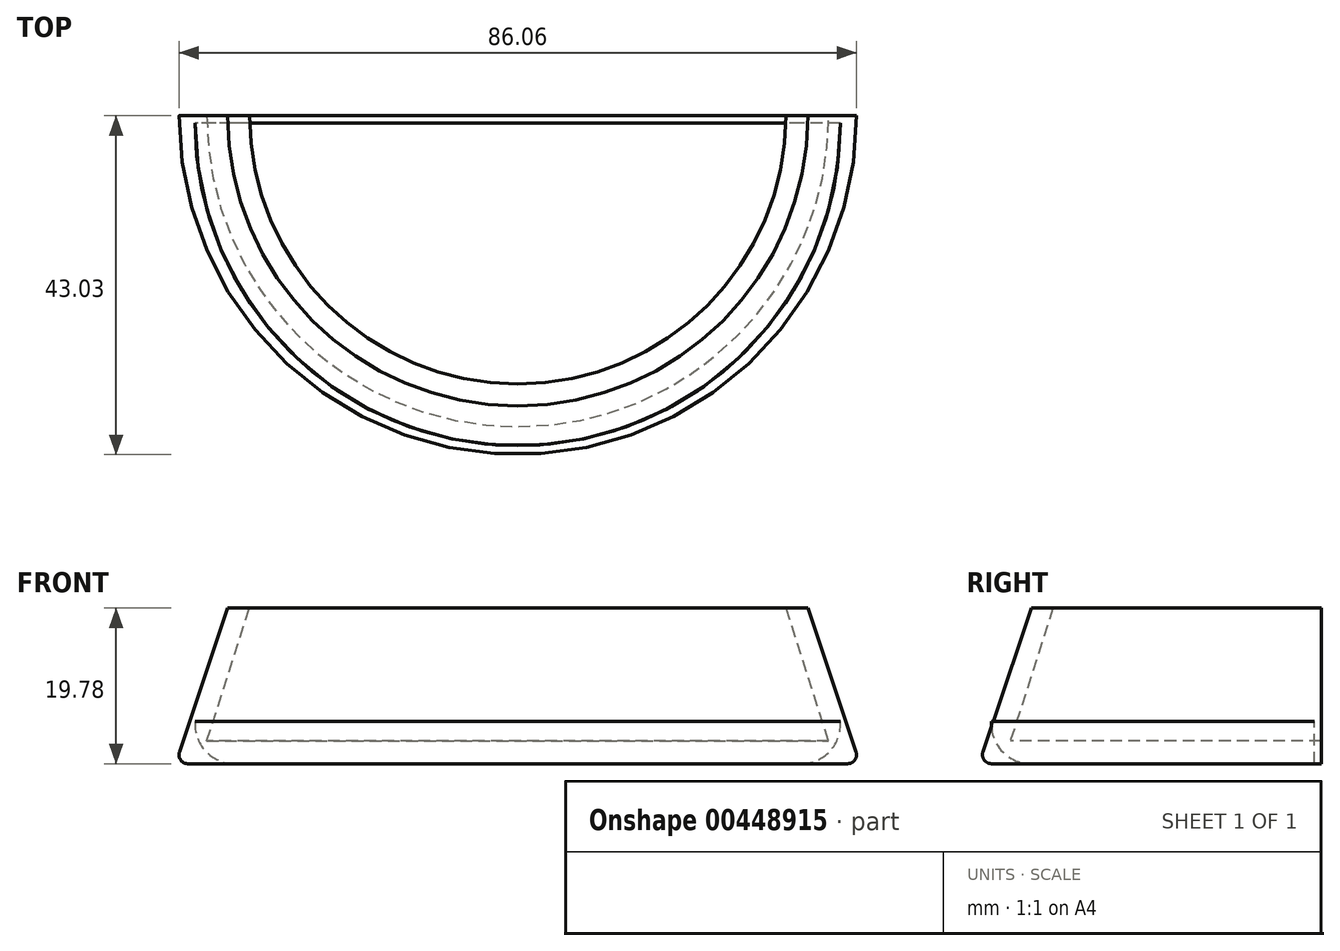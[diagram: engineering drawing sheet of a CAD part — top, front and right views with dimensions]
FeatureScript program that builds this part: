
annotation { "Feature Type Name" : "Feature", "Feature Type Description" : "" }
export const myFeature = defineFeature(function(context is Context, id is Id, definition is map)
    precondition{}
    {
        {
            var Q0;
            Q0=qCreatedBy(makeId("Front.planeOp"),FACE);
            cPlane(context, id + "F0", {"entities" : qUnion([Q0]), "cplaneType" : CPlaneType.OFFSET, "offset" : 0.9 * mm, "width" : 150 * mm, "height" : 150 * mm});
        }
        {
            var Q0;
            Q0=qCreatedBy(makeId("Front.planeOp"),FACE);
            var sketch = newSketch(context, id + "F1", { "sketchPlane" : qUnion([Q0])});
            skLineSegment(sketch, "E0", {"start": v(-43.47, 0) * mm, "end": v(0, 0) * mm});
            skLineSegment(sketch, "E1", {"start": v(0, 0) * mm, "end": v(0, 2.9) * mm});
            skLineSegment(sketch, "E2", {"start": v(0, 2.9) * mm, "end": v(-39.5, 2.9) * mm});
            skLineSegment(sketch, "E3", {"start": v(-39.5, 2.9) * mm, "end": v(-34.07, 19.78) * mm});
            skLineSegment(sketch, "E4", {"start": v(-34.07, 19.78) * mm, "end": v(-36.84, 19.78) * mm});
            skLineSegment(sketch, "E5", {"start": v(-36.84, 19.78) * mm, "end": v(-43.47, 0) * mm});
            skSolve(sketch);
        }
        {
            var Q0;
            Q0=makeQuery(id+"F1.imprint","IMPRINT",FACE,{"disambiguationData":[TD([[makeQuery(id+"F1.imprint","IMPRINT",EDGE,{"derivedFrom":sQuery(id+"F1.wireOp",EDGE,"E0")}),1.0]])]});
            var Q1;
            Q1=sQuery(id+"F1.wireOp",EDGE,"E1");
            revolve(context, id + "F2", {"entities" : qUnion([Q0]), "axis" : qUnion([Q1]), "revolveType" : RevolveType.ONE_DIRECTION, "angle" : 180 * degree});
        }
        {
            var Q0;
            Q0=makeQuery(id+"F2.opRevolve","SWEPT_EDGE",EDGE,{"disambiguationData":[OSD([sQuery(id+"F1.wireOp",EDGE,"E0"),sQuery(id+"F1.wireOp",EDGE,"E5")])]});
            fillet(context, id + "F3", {"entities" : qUnion([Q0]), "radius" : 1.12 * mm, "tangentPropagation" : true, "allowEdgeOverflow" : false});
        }
        {
            var Q0;
            Q0=qCreatedBy(id+"F0.planeOp",FACE);
            var sketch = newSketch(context, id + "F4", { "sketchPlane" : qUnion([Q0])});
            skLineSegment(sketch, "E6", {"start": v(0, 1.2) * mm, "end": v(0, 0) * mm});
            skLineSegment(sketch, "E7", {"start": v(-42.87, 0) * mm, "end": v(0, 0) * mm});
            skLineSegment(sketch, "E8", {"start": v(0, 1.2) * mm, "end": v(0, 6) * mm});
            skLineSegment(sketch, "E9", {"start": v(-40.98, 5.4) * mm, "end": v(-42.87, 0) * mm});
            skLineSegment(sketch, "E10", {"start": v(-40.98, 5.4) * mm, "end": v(0, 5.4) * mm});
            skPoint(sketch, "E10.endSnap0", {"position": v(0, 6) * mm});
            skPoint(sketch, "E11.orphan", {"position": v(0, 10.8) * mm});
            skPoint(sketch, "E12.orphan", {"position": v(-39.09, 10.8) * mm});
            skSolve(sketch);
        }
        {
            var Q0;
            Q0 = qSketchRegion(id + "F4", true);
            var Q1;
            Q1=sQuery(id+"F4.wireOp",EDGE,"E8");
            revolve(context, id + "F5", {"entities" : qUnion([Q0]), "axis" : qUnion([Q1]), "revolveType" : RevolveType.ONE_DIRECTION, "angle" : 180 * degree});
        }
        {
            var Q0;
            Q0=makeQuery(id+"F5.opRevolve","SWEPT_EDGE",EDGE,{"disambiguationData":[OSD([sQuery(id+"F4.wireOp",EDGE,"E7"),sQuery(id+"F4.wireOp",EDGE,"E9")])]});
            fillet(context, id + "F6", {"entities" : qUnion([Q0]), "radius" : 5 * mm, "tangentPropagation" : true, "allowEdgeOverflow" : false});
        }
    });
